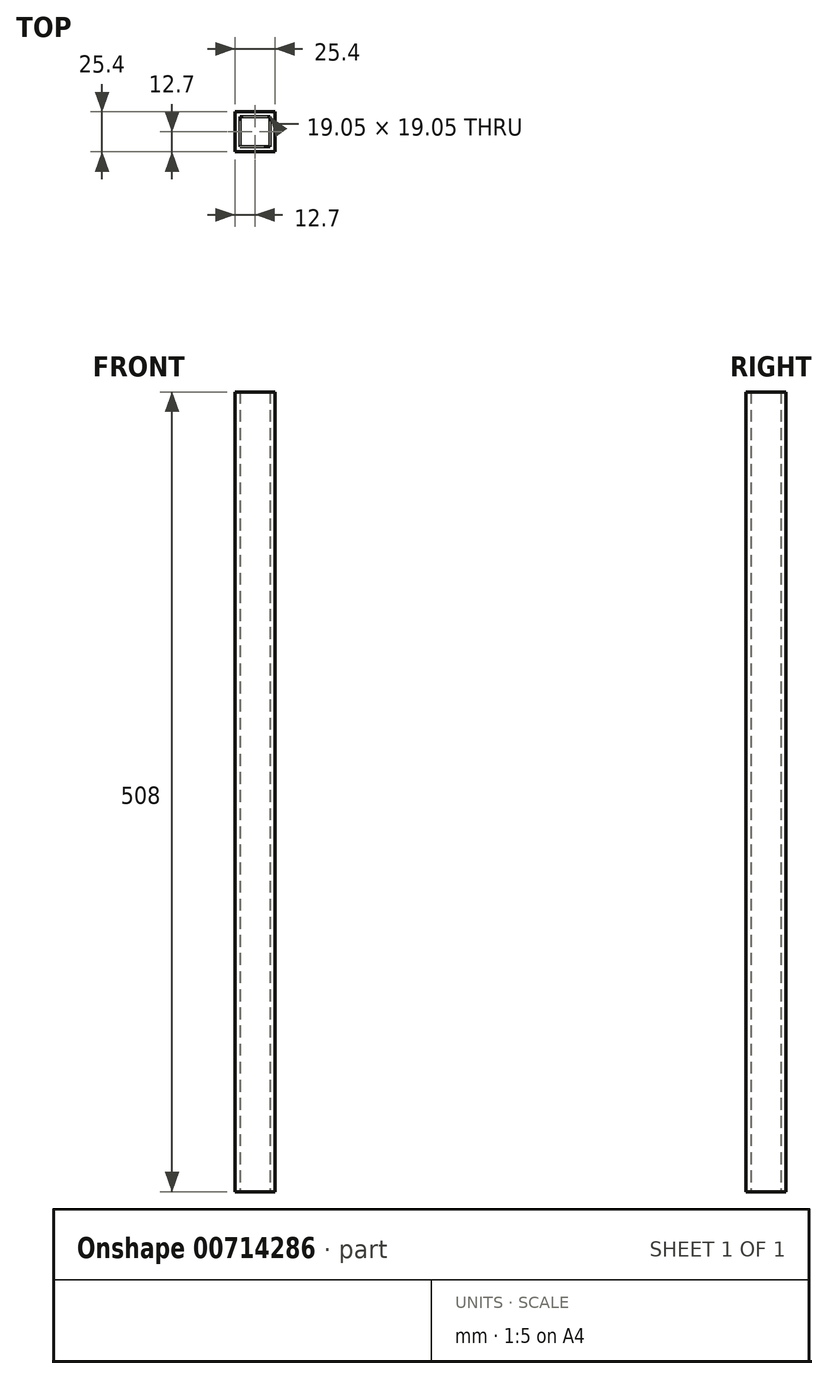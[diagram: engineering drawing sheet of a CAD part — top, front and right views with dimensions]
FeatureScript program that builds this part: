
annotation { "Feature Type Name" : "Feature", "Feature Type Description" : "" }
export const myFeature = defineFeature(function(context is Context, id is Id, definition is map)
    precondition{}
    {
        {
            var Q0;
            Q0=qCreatedBy(makeId("Top.planeOp"),FACE);
            var sketch = newSketch(context, id + "F0", { "sketchPlane" : qUnion([Q0])});
            skLineSegment(sketch, "E0.bottom", {"start": v(12.7, 12.7) * mm, "end": v(-12.7, 12.7) * mm});
            skLineSegment(sketch, "E0.top", {"start": v(12.7, -12.7) * mm, "end": v(-12.7, -12.7) * mm});
            skLineSegment(sketch, "E0.left", {"start": v(12.7, 12.7) * mm, "end": v(12.7, -12.7) * mm});
            skLineSegment(sketch, "E0.right", {"start": v(-12.7, 12.7) * mm, "end": v(-12.7, -12.7) * mm});
            skPoint(sketch, "E0.middle", {"position": v(0, 0) * mm});
            skLineSegment(sketch, "E1.0", {"start": v(9.53, 9.53) * mm, "end": v(9.53, -9.52) * mm});
            skLineSegment(sketch, "E1.1", {"start": v(9.53, 9.53) * mm, "end": v(-9.53, 9.53) * mm});
            skLineSegment(sketch, "E1.2", {"start": v(-9.53, 9.53) * mm, "end": v(-9.53, -9.52) * mm});
            skLineSegment(sketch, "E1.3", {"start": v(9.53, -9.52) * mm, "end": v(-9.53, -9.52) * mm});
            skSolve(sketch);
        }
        {
            var Q0;
            Q0 = qSketchRegion(id + "F0", true);
            extrude(context, id + "F1", {"entities" : qUnion([Q0]), "depth" : 508 * mm, "offsetDistance" : 25.4 * mm});
        }
    });
